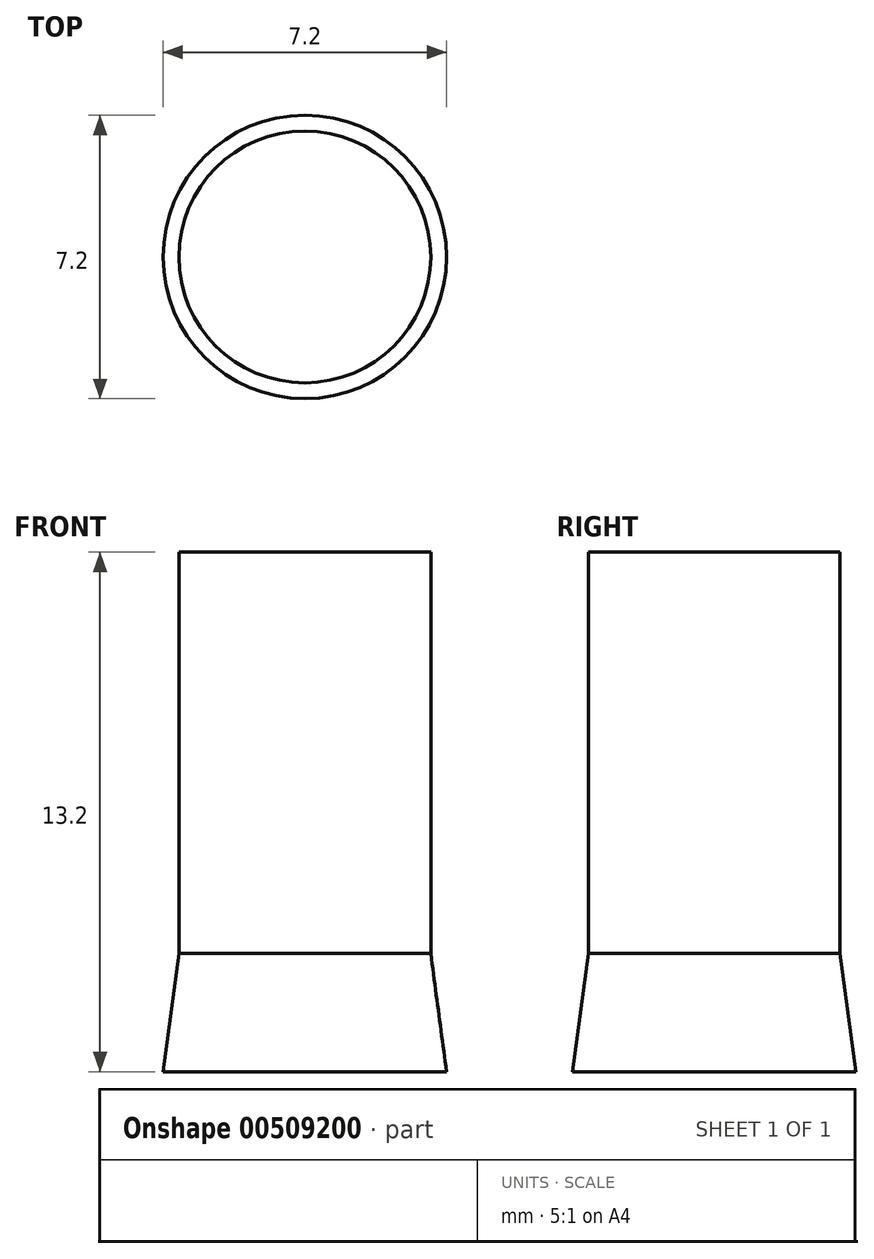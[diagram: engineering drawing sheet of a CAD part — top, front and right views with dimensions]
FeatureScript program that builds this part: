
annotation { "Feature Type Name" : "Feature", "Feature Type Description" : "" }
export const myFeature = defineFeature(function(context is Context, id is Id, definition is map)
    precondition{}
    {
        {
            var Q0;
            Q0=qCreatedBy(makeId("Front.planeOp"),FACE);
            var sketch = newSketch(context, id + "F0", { "sketchPlane" : qUnion([Q0])});
            skLineSegment(sketch, "E0", {"start": v(0, 0) * mm, "end": v(0, 8.4) * mm});
            skLineSegment(sketch, "E1", {"start": v(0, 0) * mm, "end": v(0, 5.1) * mm});
            skLineSegment(sketch, "E2", {"start": v(0, 0) * mm, "end": v(-3.2, 0) * mm});
            skLineSegment(sketch, "E3", {"start": v(-3.2, 0) * mm, "end": v(-3.2, 5.1) * mm});
            skLineSegment(sketch, "E4", {"start": v(-3.2, 5.1) * mm, "end": v(0, 5.1) * mm});
            skLineSegment(sketch, "E5", {"start": v(-3.2, 5.1) * mm, "end": v(-3.5, 5.1) * mm});
            skLineSegment(sketch, "E6", {"start": v(0, 8.4) * mm, "end": v(0, 14.4) * mm});
            skLineSegment(sketch, "E7", {"start": v(-3.5, 5.1) * mm, "end": v(0, 14.4) * mm});
            skLineSegment(sketch, "E8", {"start": v(0, 8.4) * mm, "end": v(-2.26, 8.4) * mm});
            skLineSegment(sketch, "E9", {"start": v(0, 0) * mm, "end": v(0, -5.1) * mm});
            skLineSegment(sketch, "E10", {"start": v(0, -5.1) * mm, "end": v(-3.2, -5.1) * mm});
            skLineSegment(sketch, "E11", {"start": v(-3.2, -5.1) * mm, "end": v(-3.2, 0) * mm});
            skLineSegment(sketch, "E12", {"start": v(0, -5.1) * mm, "end": v(0, -8.1) * mm});
            skLineSegment(sketch, "E13", {"start": v(0, -8.1) * mm, "end": v(-3.6, -8.1) * mm});
            skLineSegment(sketch, "E14", {"start": v(-3.2, -5.1) * mm, "end": v(-3.6, -8.1) * mm});
            skSolve(sketch);
        }
        {
            var Q0;
            Q0=makeQuery(id+"F0.imprint","IMPRINT",FACE,{"disambiguationData":[TD([[makeQuery(id+"F0.imprint","IMPRINT",EDGE,{"derivedFrom":sQuery(id+"F0.wireOp",EDGE,"E0")}),1.0]])]});
            var Q1;
            Q1=makeQuery(id+"F0.imprint","IMPRINT",FACE,{"disambiguationData":[TD([[makeQuery(id+"F0.imprint","IMPRINT",EDGE,{"derivedFrom":sQuery(id+"F0.wireOp",EDGE,"E1")}),1.0]])]});
            var Q2;
            Q2=makeQuery(id+"F0.imprint","IMPRINT",FACE,{"disambiguationData":[TD([[makeQuery(id+"F0.imprint","IMPRINT",EDGE,{"derivedFrom":sQuery(id+"F0.wireOp",EDGE,"E2")}),1.0]])]});
            var Q3;
            {var subQ0=sQuery(id+"F0.wireOp",EDGE,"E10");Q3=makeQuery(id+"F0.imprint","IMPRINT",FACE,{"disambiguationData":[TD([[makeQuery(id+"F0.imprint","IMPRINT",EDGE,{"derivedFrom":subQ0}),1.0]])]});}
            var Q4;
            {var subQ0=sQuery(id+"F0.wireOp",EDGE,"E12");Q4=makeQuery(id+"F0.imprint","IMPRINT",FACE,{"disambiguationData":[TD([[makeQuery(id+"F0.imprint","IMPRINT",EDGE,{"derivedFrom":subQ0}),-1.0]])]});}
            var Q5;
            {var subQ0=sQuery(id+"F0.wireOp",EDGE,"U2n0Z7tD-sUGo-40HQ-I8jl-J8u7tjTmNh0A");var subQ1=sQuery(id+"F0.wireOp",EDGE,"E13");var subQ2=makeQuery(id+"F0.imprint","INTERSECT",VERTEX,{"derivedFrom":[subQ1,subQ0]});Q5=makeQuery(id+"F0.imprint","IMPRINT",FACE,{"disambiguationData":[TD([[makeQuery(id+"F0.imprint","IMPRINT",EDGE,{"disambiguationData":[TD([[subQ2,1.0]])],"derivedFrom":subQ1}),-1.0]])]});}
            var Q6;
            Q6=sQuery(id+"F0.wireOp",EDGE,"E9");
            revolve(context, id + "F1", {"entities" : qUnion([Q0, Q1, Q2, Q3, Q4, Q5]), "axis" : qUnion([Q6]), "revolveType" : RevolveType.FULL});
        }
    });
